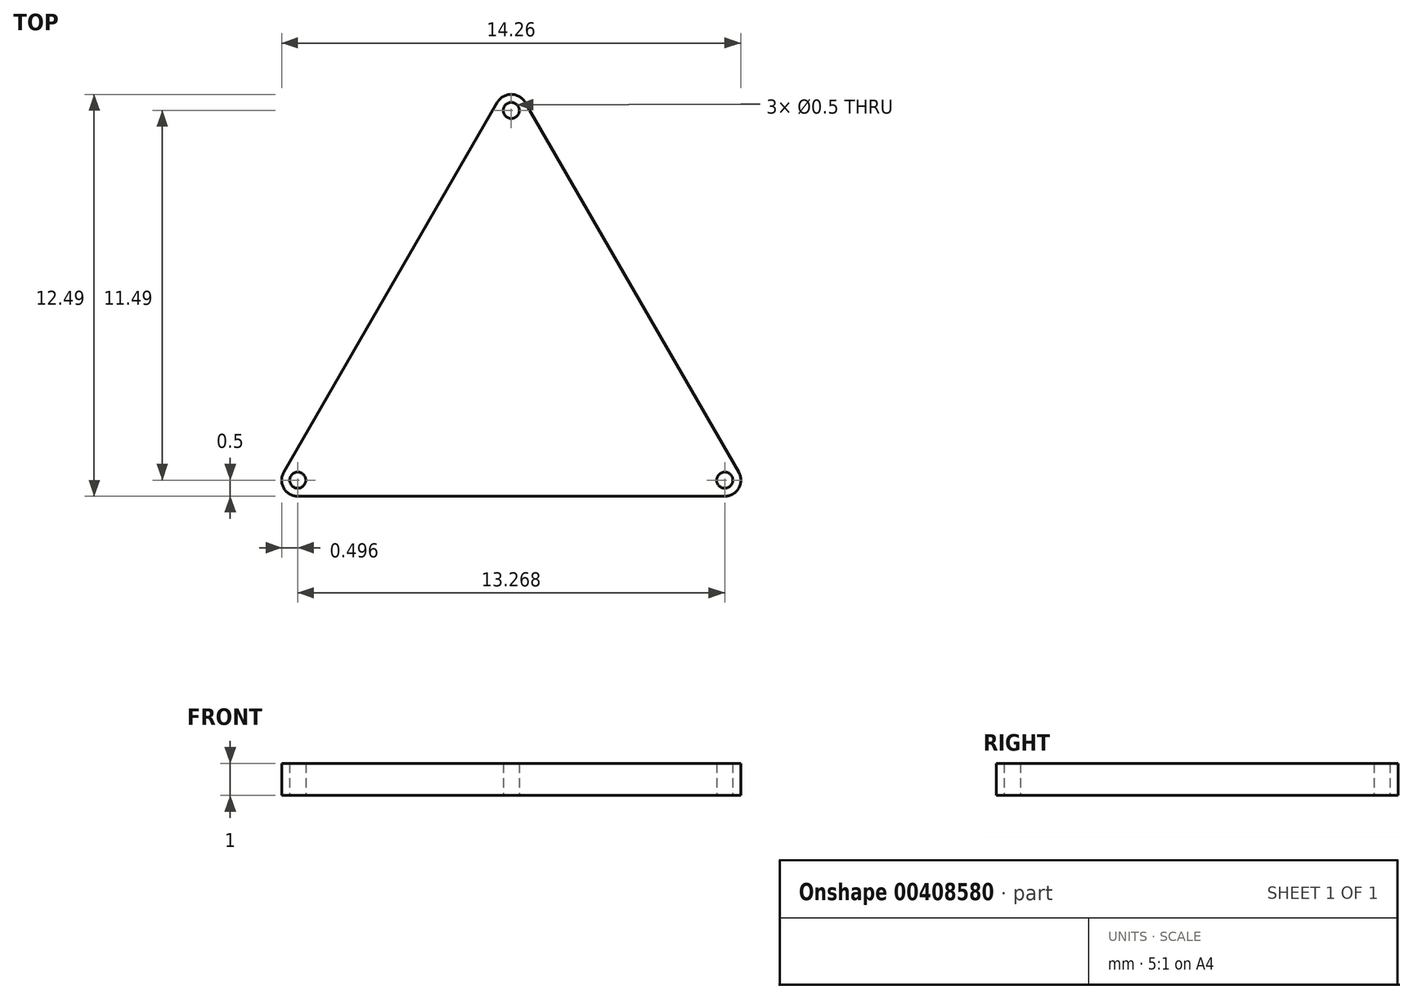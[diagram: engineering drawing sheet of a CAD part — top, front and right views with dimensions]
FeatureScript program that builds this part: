
annotation { "Feature Type Name" : "Feature", "Feature Type Description" : "" }
export const myFeature = defineFeature(function(context is Context, id is Id, definition is map)
    precondition{}
    {
        {
            var Q0;
            Q0=qCreatedBy(makeId("Top.planeOp"),FACE);
            var sketch = newSketch(context, id + "F0", { "sketchPlane" : qUnion([Q0])});
            skLineSegment(sketch, "E0", {"start": v(-0.43, 7.24) * mm, "end": v(-7.07, -4.25) * mm});
            skLineSegment(sketch, "E1", {"start": v(-6.63, -5) * mm, "end": v(6.63, -5) * mm});
            skLineSegment(sketch, "E2", {"start": v(7.07, -4.25) * mm, "end": v(0.43, 7.24) * mm});
            skPoint(sketch, "E3.visualSharp", {"position": v(0, 8) * mm});
            skArc(sketch, "E3.filletArc", {"start": v(0.43, 7.24) * mm, "mid": v(0, 7.5) * mm, "end": v(-0.43, 7.24) * mm});
            skPoint(sketch, "E4.visualSharp", {"position": v(-7.5, -5) * mm});
            skArc(sketch, "E4.filletArc", {"start": v(-7.07, -4.25) * mm, "mid": v(-7.07, -4.75) * mm, "end": v(-6.63, -5) * mm});
            skPoint(sketch, "E5.visualSharp", {"position": v(7.5, -5) * mm});
            skArc(sketch, "E5.filletArc", {"start": v(6.63, -5) * mm, "mid": v(7.07, -4.75) * mm, "end": v(7.07, -4.25) * mm});
            skCircle(sketch, "E6", {"center": v(-6.63, -4.5) * mm, "radius": 0.25 * mm});
            skCircle(sketch, "E7", {"center": v(6.63, -4.5) * mm, "radius": 0.25 * mm});
            skCircle(sketch, "E8", {"center": v(0, 7) * mm, "radius": 0.25 * mm});
            skSolve(sketch);
        }
        {
            var Q0;
            Q0 = qSketchRegion(id + "F0", true);
            extrude(context, id + "F1", {"entities" : qUnion([Q0]), "depth" : 1 * mm, "offsetDistance" : 25 * mm});
        }
    });
